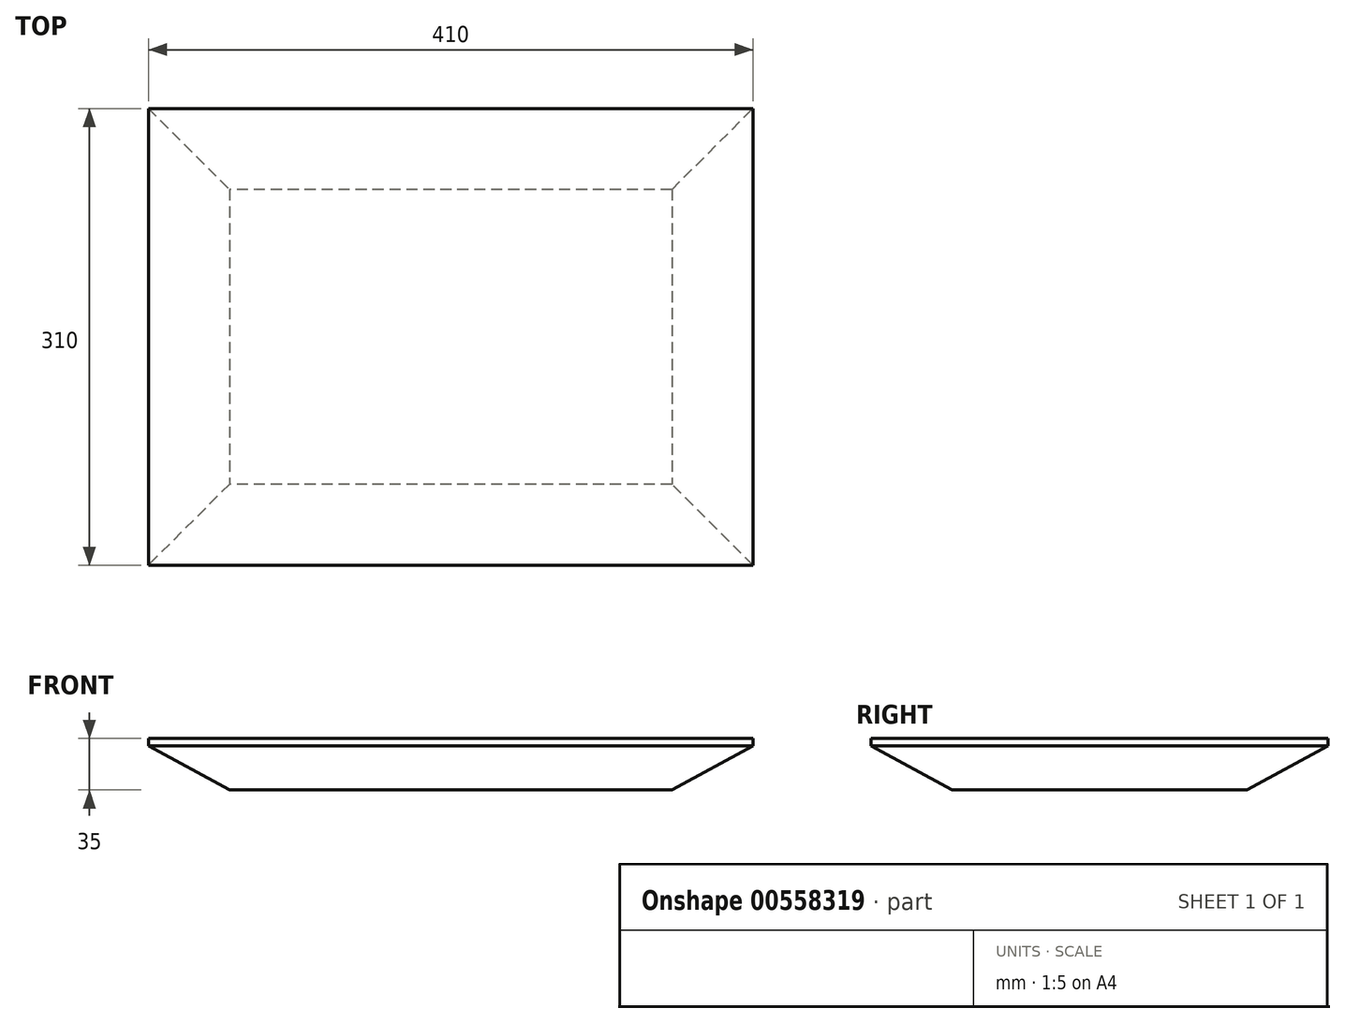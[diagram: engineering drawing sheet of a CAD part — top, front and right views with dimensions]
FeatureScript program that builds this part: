
annotation { "Feature Type Name" : "Feature", "Feature Type Description" : "" }
export const myFeature = defineFeature(function(context is Context, id is Id, definition is map)
    precondition{}
    {
        {
            var Q0;
            Q0=qCreatedBy(makeId("Top.planeOp"),FACE);
            var sketch = newSketch(context, id + "F0", { "sketchPlane" : qUnion([Q0])});
            skLineSegment(sketch, "E0.bottom", {"start": v(205, -155) * mm, "end": v(-205, -155) * mm});
            skLineSegment(sketch, "E0.top", {"start": v(205, 155) * mm, "end": v(-205, 155) * mm});
            skLineSegment(sketch, "E0.left", {"start": v(205, -155) * mm, "end": v(205, 155) * mm});
            skLineSegment(sketch, "E0.right", {"start": v(-205, -155) * mm, "end": v(-205, 155) * mm});
            skPoint(sketch, "E0.middle", {"position": v(0, 0) * mm});
            skSolve(sketch);
        }
        {
            var Q0;
            Q0=qSketchRegion(id+"F0",true);
            extrude(context, id + "F1", {"entities" : qUnion([Q0]), "depth" : 35 * mm, "offsetDistance" : 25 * mm});
        }
        {
            var Q0;
            Q0=makeQuery(id+"F1.opExtrude","SWEPT_FACE",FACE,{"disambiguationData":[OSD([sQuery(id+"F0.wireOp",EDGE,"E0.bottom")])]});
            var sketch = newSketch(context, id + "F2", { "sketchPlane" : qUnion([Q0])});
            skLineSegment(sketch, "E1", {"start": v(-150, 0) * mm, "end": v(-205, 30) * mm});
            skLineSegment(sketch, "E2", {"start": v(-205, 30) * mm, "end": v(-247.47, 11.41) * mm});
            skLineSegment(sketch, "E3", {"start": v(-247.47, 11.41) * mm, "end": v(-186.29, -45.12) * mm});
            skLineSegment(sketch, "E4", {"start": v(-186.29, -45.12) * mm, "end": v(-150, 0) * mm});
            skSolve(sketch);
        }
        {
            var Q0;
            Q0=qSketchRegion(id+"F2",true);
            extrude(context, id + "F3", {"entities" : qUnion([Q0]), "oppositeDirection" : true, "depth" : 413 * mm, "offsetDistance" : 25 * mm});
        }
        {
            var Q0;
            Q0=makeQuery(id+"F3.opExtrude","SWEPT_BODY",BODY,{"disambiguationData":[OSD([sQuery(id+"F2.wireOp",EDGE,"E1"),sQuery(id+"F2.wireOp",EDGE,"E2"),sQuery(id+"F2.wireOp",EDGE,"E3"),sQuery(id+"F2.wireOp",EDGE,"E4")])]});
            var Q1;
            Q1=qCreatedBy(makeId("Right.planeOp"),FACE);
            mirror(context, id + "F4", {"entities" : qUnion([Q0]), "mirrorPlane" : qUnion([Q1])});
        }
        {
            var Q0;
            Q0=makeQuery(id+"F3.opExtrude","SWEPT_BODY",BODY,{"disambiguationData":[OSD([sQuery(id+"F2.wireOp",EDGE,"E1"),sQuery(id+"F2.wireOp",EDGE,"E2"),sQuery(id+"F2.wireOp",EDGE,"E3"),sQuery(id+"F2.wireOp",EDGE,"E4")])]});
            var Q1;
            Q1=makeQuery(id+"F4.opPattern","COPY",BODY,{"derivedFrom":makeQuery(id+"F3.opExtrude","SWEPT_BODY",BODY,{"disambiguationData":[OSD([sQuery(id+"F2.wireOp",EDGE,"E1"),sQuery(id+"F2.wireOp",EDGE,"E2"),sQuery(id+"F2.wireOp",EDGE,"E3"),sQuery(id+"F2.wireOp",EDGE,"E4")])]}),"instanceName":"1"});
            var Q2;
            Q2=makeQuery(id+"F1.opExtrude","SWEPT_BODY",BODY,{"disambiguationData":[OSD([sQuery(id+"F0.wireOp",EDGE,"E0.bottom"),sQuery(id+"F0.wireOp",EDGE,"E0.top"),sQuery(id+"F0.wireOp",EDGE,"E0.left"),sQuery(id+"F0.wireOp",EDGE,"E0.right")])]});
            booleanBodies(context, id + "F5", {"operationType" : BooleanOperationType.SUBTRACTION, "tools" : qUnion([Q0, Q1]), "targets" : qUnion([Q2])});
        }
        {
            var Q0;
            Q0=makeQuery(id+"F1.opExtrude","SWEPT_FACE",FACE,{"disambiguationData":[OSD([sQuery(id+"F0.wireOp",EDGE,"E0.right")])]});
            var sketch = newSketch(context, id + "F6", { "sketchPlane" : qUnion([Q0])});
            skLineSegment(sketch, "E5", {"start": v(-100, 0) * mm, "end": v(-155, 30) * mm});
            skLineSegment(sketch, "E6", {"start": v(-155, 30) * mm, "end": v(-189.2, 15.52) * mm});
            skLineSegment(sketch, "E7", {"start": v(-189.2, 15.52) * mm, "end": v(-155, -27.47) * mm});
            skLineSegment(sketch, "E8", {"start": v(-155, -27.47) * mm, "end": v(-100, 0) * mm});
            skSolve(sketch);
        }
        {
            var Q0;
            Q0=qSketchRegion(id+"F6",true);
            extrude(context, id + "F7", {"entities" : qUnion([Q0]), "oppositeDirection" : true, "depth" : 455 * mm, "offsetDistance" : 25 * mm});
        }
        {
            var Q0;
            Q0=makeQuery(id+"F7.opExtrude","SWEPT_BODY",BODY,{"disambiguationData":[OSD([sQuery(id+"F6.wireOp",EDGE,"E5"),sQuery(id+"F6.wireOp",EDGE,"E6"),sQuery(id+"F6.wireOp",EDGE,"E7"),sQuery(id+"F6.wireOp",EDGE,"E8")])]});
            var Q1;
            Q1=qCreatedBy(makeId("Front.planeOp"),FACE);
            mirror(context, id + "F8", {"entities" : qUnion([Q0]), "mirrorPlane" : qUnion([Q1])});
        }
        {
            var Q0;
            Q0=makeQuery(id+"F7.opExtrude","SWEPT_BODY",BODY,{"disambiguationData":[OSD([sQuery(id+"F6.wireOp",EDGE,"E5"),sQuery(id+"F6.wireOp",EDGE,"E6"),sQuery(id+"F6.wireOp",EDGE,"E7"),sQuery(id+"F6.wireOp",EDGE,"E8")])]});
            var Q1;
            Q1=makeQuery(id+"F8.opPattern","COPY",BODY,{"derivedFrom":makeQuery(id+"F7.opExtrude","SWEPT_BODY",BODY,{"disambiguationData":[OSD([sQuery(id+"F6.wireOp",EDGE,"E5"),sQuery(id+"F6.wireOp",EDGE,"E6"),sQuery(id+"F6.wireOp",EDGE,"E7"),sQuery(id+"F6.wireOp",EDGE,"E8")])]}),"instanceName":"1"});
            var Q2;
            Q2=makeQuery(id+"F1.opExtrude","SWEPT_BODY",BODY,{"disambiguationData":[OSD([sQuery(id+"F0.wireOp",EDGE,"E0.bottom"),sQuery(id+"F0.wireOp",EDGE,"E0.top"),sQuery(id+"F0.wireOp",EDGE,"E0.left"),sQuery(id+"F0.wireOp",EDGE,"E0.right")])]});
            booleanBodies(context, id + "F9", {"operationType" : BooleanOperationType.SUBTRACTION, "tools" : qUnion([Q0, Q1]), "targets" : qUnion([Q2])});
        }
    });
